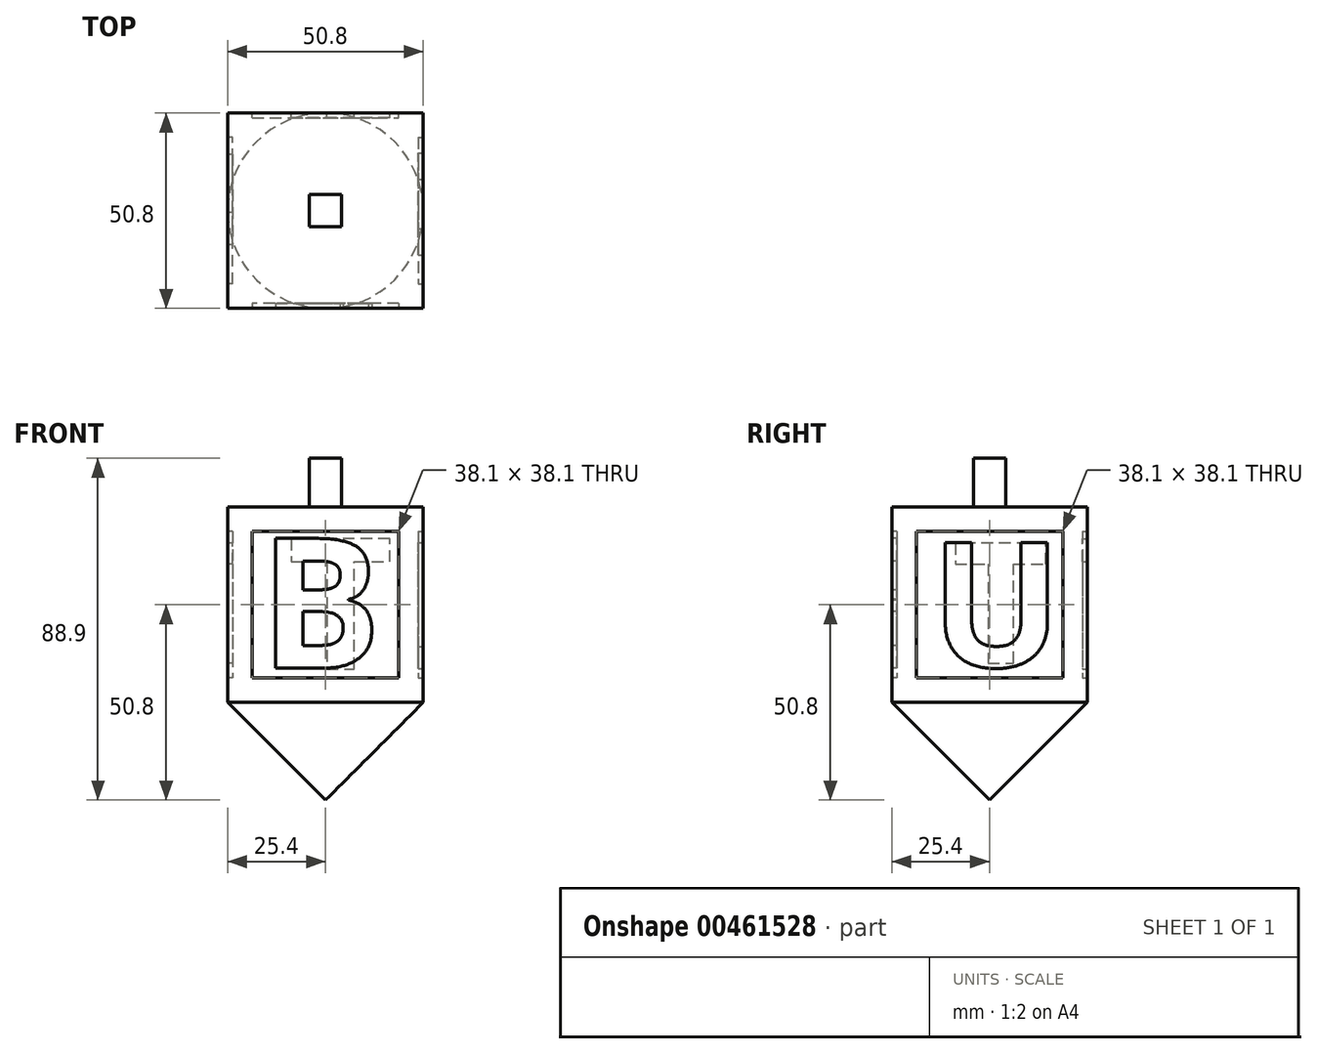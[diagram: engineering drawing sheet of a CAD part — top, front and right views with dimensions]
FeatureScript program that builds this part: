
annotation { "Feature Type Name" : "Feature", "Feature Type Description" : "" }
export const myFeature = defineFeature(function(context is Context, id is Id, definition is map)
    precondition{}
    {
        {
            var Q0;
            Q0=qCreatedBy(makeId("Top.planeOp"),FACE);
            var sketch = newSketch(context, id + "F0", { "sketchPlane" : qUnion([Q0])});
            skLineSegment(sketch, "E0.bottom", {"start": v(25.4, 25.4) * mm, "end": v(-25.4, 25.4) * mm});
            skLineSegment(sketch, "E0.top", {"start": v(25.4, -25.4) * mm, "end": v(-25.4, -25.4) * mm});
            skLineSegment(sketch, "E0.left", {"start": v(25.4, 25.4) * mm, "end": v(25.4, -25.4) * mm});
            skLineSegment(sketch, "E0.right", {"start": v(-25.4, 25.4) * mm, "end": v(-25.4, -25.4) * mm});
            skPoint(sketch, "E0.middle", {"position": v(0, 0) * mm});
            skSolve(sketch);
        }
        {
            var Q0;
            Q0=makeQuery(id+"F0.imprint","IMPRINT",FACE,{"disambiguationData":[TD([[makeQuery(id+"F0.imprint","IMPRINT",EDGE,{"derivedFrom":sQuery(id+"F0.wireOp",EDGE,"E0.bottom")}),1.0]])]});
            extrude(context, id + "F1", {"entities" : qUnion([Q0]), "depth" : 50.8 * mm, "offsetDistance" : 25.4 * mm});
        }
        {
            var Q0;
            Q0=makeQuery(id+"F1.opExtrude","SWEPT_FACE",FACE,{"disambiguationData":[OSD([sQuery(id+"F0.wireOp",EDGE,"E0.top")])]});
            var sketch = newSketch(context, id + "F2", { "sketchPlane" : qUnion([Q0])});
            skLineSegment(sketch, "E1.bottom", {"start": v(19.05, 44.45) * mm, "end": v(-19.05, 44.45) * mm});
            skLineSegment(sketch, "E1.top", {"start": v(19.05, 6.35) * mm, "end": v(-19.05, 6.35) * mm});
            skLineSegment(sketch, "E1.left", {"start": v(19.05, 44.45) * mm, "end": v(19.05, 6.35) * mm});
            skLineSegment(sketch, "E1.right", {"start": v(-19.05, 44.45) * mm, "end": v(-19.05, 6.35) * mm});
            skPoint(sketch, "E1.middle", {"position": v(0, 25.4) * mm});
            skPoint(sketch, "E1.middle.positionSnap0", {"position": v(-25.4, 25.4) * mm});
            skPoint(sketch, "E1.middle.positionSnap1", {"position": v(0, 0) * mm});
            skPoint(sketch, "E1.centerSnap0", {"position": v(-25.4, 25.4) * mm});
            skPoint(sketch, "E1.centerSnap1", {"position": v(0, 0) * mm});
            skText(sketch, "E2", { "text": "B", "fontName": "OpenSans-Bold.ttf"});
            const initialGuessF2  = {"E2": [-0.01723, 0.00894, 1, 0, 0.03403]};
            skSetInitialGuess(sketch, initialGuessF2);
            skSolve(sketch);
        }
        {
            var Q0;
            Q0=makeQuery(id+"F2.imprint","IMPRINT",FACE,{"disambiguationData":[TD([[makeQuery(id+"F2.imprint","IMPRINT",EDGE,{"derivedFrom":sQuery(id+"F2.wireOp",EDGE,"E1.bottom")}),1.0]])]});
            var Q1;
            Q1=makeQuery(id+"F2.imprint","IMPRINT",FACE,{"disambiguationData":[TD([[makeQuery(id+"F2.imprint","IMPRINT",EDGE,{"derivedFrom":sQuery(id+"F2.wireOp",EDGE,"E2.sketch_text.stroke-12")}),1.0]])]});
            var Q2;
            Q2=makeQuery(id+"F2.imprint","IMPRINT",FACE,{"disambiguationData":[TD([[makeQuery(id+"F2.imprint","IMPRINT",EDGE,{"derivedFrom":sQuery(id+"F2.wireOp",EDGE,"E2.sketch_text.stroke-19")}),1.0]])]});
            extrude(context, id + "F3", {"entities" : qUnion([Q0, Q1, Q2]), "operationType" : NewBodyOperationType.REMOVE, "oppositeDirection" : true, "depth" : 1.27 * mm, "offsetDistance" : 25.4 * mm});
        }
        {
            var Q0;
            Q0=makeQuery(id+"F1.opExtrude","SWEPT_FACE",FACE,{"disambiguationData":[OSD([sQuery(id+"F0.wireOp",EDGE,"E0.left")])]});
            var sketch = newSketch(context, id + "F4", { "sketchPlane" : qUnion([Q0])});
            skLineSegment(sketch, "E3.bottom", {"start": v(19.05, 44.45) * mm, "end": v(-19.05, 44.45) * mm});
            skLineSegment(sketch, "E3.top", {"start": v(19.05, 6.35) * mm, "end": v(-19.05, 6.35) * mm});
            skLineSegment(sketch, "E3.left", {"start": v(19.05, 44.45) * mm, "end": v(19.05, 6.35) * mm});
            skLineSegment(sketch, "E3.right", {"start": v(-19.05, 44.45) * mm, "end": v(-19.05, 6.35) * mm});
            skPoint(sketch, "E3.middle", {"position": v(0, 25.4) * mm});
            skPoint(sketch, "E3.middle.positionSnap0", {"position": v(25.4, 25.4) * mm});
            skPoint(sketch, "E3.centerSnap0", {"position": v(25.4, 25.4) * mm});
            skText(sketch, "E4", { "text": "U", "fontName": "OpenSans-Bold.ttf"});
            const initialGuessF4  = {"E4": [-0.01537, 0.00926, 1, 0, 0.03265]};
            skSetInitialGuess(sketch, initialGuessF4);
            skSolve(sketch);
        }
        {
            var Q0;
            Q0=makeQuery(id+"F4.imprint","IMPRINT",FACE,{"disambiguationData":[TD([[makeQuery(id+"F4.imprint","IMPRINT",EDGE,{"derivedFrom":sQuery(id+"F4.wireOp",EDGE,"E3.bottom")}),1.0]])]});
            extrude(context, id + "F5", {"entities" : qUnion([Q0]), "operationType" : NewBodyOperationType.REMOVE, "oppositeDirection" : true, "depth" : 1.27 * mm, "offsetDistance" : 25.4 * mm});
        }
        {
            var Q0;
            Q0=makeQuery(id+"F1.opExtrude","SWEPT_FACE",FACE,{"disambiguationData":[OSD([sQuery(id+"F0.wireOp",EDGE,"E0.bottom")])]});
            var sketch = newSketch(context, id + "F6", { "sketchPlane" : qUnion([Q0])});
            skLineSegment(sketch, "E5.bottom", {"start": v(19.05, 44.45) * mm, "end": v(-19.05, 44.45) * mm});
            skLineSegment(sketch, "E5.top", {"start": v(19.05, 6.35) * mm, "end": v(-19.05, 6.35) * mm});
            skLineSegment(sketch, "E5.left", {"start": v(19.05, 44.45) * mm, "end": v(19.05, 6.35) * mm});
            skLineSegment(sketch, "E5.right", {"start": v(-19.05, 44.45) * mm, "end": v(-19.05, 6.35) * mm});
            skPoint(sketch, "E5.middle", {"position": v(0, 25.4) * mm});
            skPoint(sketch, "E5.middle.positionSnap0", {"position": v(-25.4, 25.4) * mm});
            skPoint(sketch, "E5.centerSnap0", {"position": v(-25.4, 25.4) * mm});
            skText(sketch, "E6", { "text": "T", "fontName": "OpenSans-Bold.ttf"});
            const initialGuessF6  = {"E6": [-0.01766, 0.00869, 1, 0, 0.03418]};
            skSetInitialGuess(sketch, initialGuessF6);
            skSolve(sketch);
        }
        {
            var Q0;
            Q0 = qSketchRegion(id + "F6", true);
            extrude(context, id + "F7", {"entities" : qUnion([Q0]), "operationType" : NewBodyOperationType.REMOVE, "oppositeDirection" : true, "depth" : 1.27 * mm, "offsetDistance" : 25.4 * mm});
        }
        {
            var Q0;
            Q0=makeQuery(id+"F1.opExtrude","SWEPT_FACE",FACE,{"disambiguationData":[OSD([sQuery(id+"F0.wireOp",EDGE,"E0.right")])]});
            var sketch = newSketch(context, id + "F8", { "sketchPlane" : qUnion([Q0])});
            skLineSegment(sketch, "E7.bottom", {"start": v(19.05, 44.45) * mm, "end": v(-19.05, 44.45) * mm});
            skLineSegment(sketch, "E7.top", {"start": v(19.05, 6.35) * mm, "end": v(-19.05, 6.35) * mm});
            skLineSegment(sketch, "E7.left", {"start": v(19.05, 44.45) * mm, "end": v(19.05, 6.35) * mm});
            skLineSegment(sketch, "E7.right", {"start": v(-19.05, 44.45) * mm, "end": v(-19.05, 6.35) * mm});
            skPoint(sketch, "E7.middle", {"position": v(0, 25.4) * mm});
            skPoint(sketch, "E7.middle.positionSnap0", {"position": v(-25.4, 25.4) * mm});
            skPoint(sketch, "E7.centerSnap0", {"position": v(-25.4, 25.4) * mm});
            skText(sketch, "E8", { "text": "T", "fontName": "OpenSans-Bold.ttf"});
            const initialGuessF8  = {"E8": [-0.01556, 0.01022, 1, 0, 0.0315]};
            skSetInitialGuess(sketch, initialGuessF8);
            skSolve(sketch);
        }
        {
            var Q0;
            Q0 = qSketchRegion(id + "F8", true);
            extrude(context, id + "F9", {"entities" : qUnion([Q0]), "operationType" : NewBodyOperationType.REMOVE, "oppositeDirection" : true, "depth" : 1.27 * mm, "offsetDistance" : 25.4 * mm});
        }
        {
            var Q0;
            Q0=makeQuery(id+"F1.opExtrude","CAP_FACE",FACE,{"disambiguationData":[OSD([sQuery(id+"F0.wireOp",EDGE,"E0.bottom"),sQuery(id+"F0.wireOp",EDGE,"E0.top"),sQuery(id+"F0.wireOp",EDGE,"E0.left"),sQuery(id+"F0.wireOp",EDGE,"E0.right")])],"isStart":false});
            var sketch = newSketch(context, id + "F10", { "sketchPlane" : qUnion([Q0])});
            skLineSegment(sketch, "E9.bottom", {"start": v(4.2, 4.2) * mm, "end": v(-4.2, 4.2) * mm});
            skLineSegment(sketch, "E9.top", {"start": v(4.2, -4.2) * mm, "end": v(-4.2, -4.2) * mm});
            skLineSegment(sketch, "E9.left", {"start": v(4.2, 4.2) * mm, "end": v(4.2, -4.2) * mm});
            skLineSegment(sketch, "E9.right", {"start": v(-4.2, 4.2) * mm, "end": v(-4.2, -4.2) * mm});
            skPoint(sketch, "E9.middle", {"position": v(0, 0) * mm});
            skSolve(sketch);
        }
        {
            var Q0;
            Q0 = qSketchRegion(id + "F10", true);
            extrude(context, id + "F11", {"entities" : qUnion([Q0]), "operationType" : NewBodyOperationType.ADD, "depth" : 12.7 * mm, "offsetDistance" : 25.4 * mm});
        }
        {
            var Q0;
            Q0=makeQuery(id+"F1.opExtrude","CAP_FACE",FACE,{"disambiguationData":[OSD([sQuery(id+"F0.wireOp",EDGE,"E0.bottom"),sQuery(id+"F0.wireOp",EDGE,"E0.top"),sQuery(id+"F0.wireOp",EDGE,"E0.left"),sQuery(id+"F0.wireOp",EDGE,"E0.right")])],"isStart":true});
            var sketch = newSketch(context, id + "F12", { "sketchPlane" : qUnion([Q0])});
            skCircle(sketch, "E10", {"center": v(0, 0) * mm, "radius": 25.4 * mm});
            skSolve(sketch);
        }
        {
            var Q0;
            {var subQ0=sQuery(id+"F12.wireOp",EDGE,"E10");var subQ1=makeQuery(id+"F12.imprint","INTERSECT",VERTEX,{"derivedFrom":[makeQuery(id+"F1.opExtrude","CAP_EDGE",EDGE,{"disambiguationData":[OSD([sQuery(id+"F0.wireOp",EDGE,"E0.top")])],"isStart":true}),subQ0]});Q0=makeQuery(id+"F12.imprint","IMPRINT",FACE,{"disambiguationData":[TD([[makeQuery(id+"F12.imprint","IMPRINT",EDGE,{"disambiguationData":[TD([[subQ1,1.0]])],"derivedFrom":subQ0}),1.0]])]});}
            extrude(context, id + "F13", {"entities" : qUnion([Q0]), "operationType" : NewBodyOperationType.ADD, "depth" : 25.4 * mm, "offsetDistance" : 25.4 * mm});
        }
        {
            var Q0;
            Q0=makeQuery(id+"F13.opExtrude","CAP_EDGE",EDGE,{"disambiguationData":[OSD([sQuery(id+"F12.wireOp",EDGE,"E10")])],"isStart":false});
            chamfer(context, id + "F14", {"entities" : qUnion([Q0]), "width" : 25.4 * mm, "tangentPropagation" : true});
        }
    });
